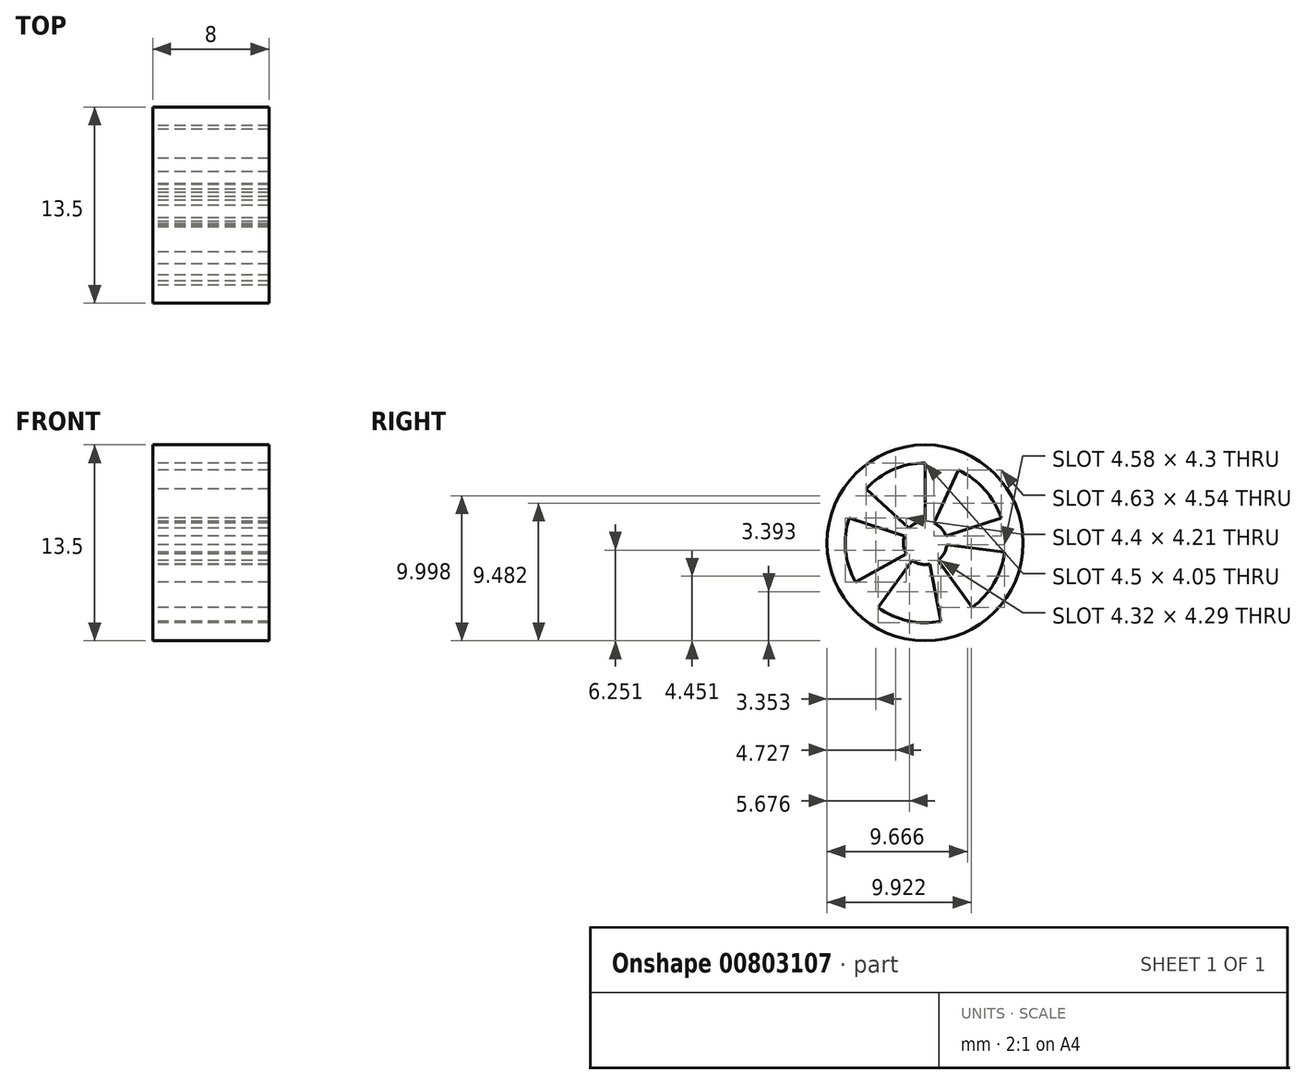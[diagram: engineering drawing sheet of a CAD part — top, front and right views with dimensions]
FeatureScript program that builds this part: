
annotation { "Feature Type Name" : "Feature", "Feature Type Description" : "" }
export const myFeature = defineFeature(function(context is Context, id is Id, definition is map)
    precondition{}
    {
        {
            var Q0;
            Q0=qCreatedBy(makeId("Right.planeOp"),FACE);
            var sketch = newSketch(context, id + "F0", { "sketchPlane" : qUnion([Q0])});
            skCircle(sketch, "E0", {"center": v(0, 0) * mm, "radius": 6.75 * mm});
            skSolve(sketch);
        }
        {
            var Q0;
            Q0=makeQuery(id+"F0.imprint","IMPRINT",FACE,{"disambiguationData":[TD([[makeQuery(id+"F0.imprint","IMPRINT",EDGE,{"derivedFrom":sQuery(id+"F0.wireOp",EDGE,"E0")}),1.0]])]});
            var sketch = newSketch(context, id + "F1", { "sketchPlane" : qUnion([Q0])});
            skCircle(sketch, "E1", {"center": v(0, 0) * mm, "radius": 5.5 * mm});
            skArc(sketch, "E2", {"start": v(0, 1.5) * mm, "mid": v(-0.3, -1.47) * mm, "end": v(0.6, 1.37) * mm});
            skLineSegment(sketch, "E3", {"start": v(0, 1.5) * mm, "end": v(0, 5.5) * mm});
            skLineSegment(sketch, "E4", {"start": v(0.6, 1.37) * mm, "end": v(2.3, 5) * mm});
            skLineSegment(sketch, "E5.1.0", {"start": v(-1.12, 1) * mm, "end": v(-4.05, 3.72) * mm});
            skLineSegment(sketch, "E5.1.1", {"start": v(-1.43, 0.46) * mm, "end": v(-5.23, 1.7) * mm});
            skLineSegment(sketch, "E5.2.0", {"start": v(-1.3, -0.76) * mm, "end": v(-4.8, -2.7) * mm});
            skLineSegment(sketch, "E5.2.1", {"start": v(-0.88, -1.21) * mm, "end": v(-3.23, -4.45) * mm});
            skLineSegment(sketch, "E5.3.0", {"start": v(0.32, -1.47) * mm, "end": v(1.08, -5.4) * mm});
            skLineSegment(sketch, "E5.3.1", {"start": v(0.88, -1.21) * mm, "end": v(3.23, -4.45) * mm});
            skLineSegment(sketch, "E5.4.0", {"start": v(1.5, -0.15) * mm, "end": v(5.46, -0.64) * mm});
            skLineSegment(sketch, "E5.4.1", {"start": v(1.43, 0.46) * mm, "end": v(5.23, 1.7) * mm});
            skSolve(sketch);
        }
        {
            var Q0;
            Q0=makeQuery(id+"F0.imprint","IMPRINT",FACE,{"disambiguationData":[TD([[makeQuery(id+"F0.imprint","IMPRINT",EDGE,{"derivedFrom":sQuery(id+"F0.wireOp",EDGE,"E0")}),1.0]])]});
            extrude(context, id + "F2", {"entities" : qUnion([Q0]), "depth" : 8 * mm, "offsetDistance" : 25 * mm});
        }
        {
            var Q0;
            {var subQ0=sQuery(id+"F1.wireOp",EDGE,"E5.2.1");Q0=makeQuery(id+"F1.imprint","IMPRINT",FACE,{"disambiguationData":[TD([[makeQuery(id+"F1.imprint","IMPRINT",EDGE,{"derivedFrom":subQ0}),1.0]])]});}
            var Q1;
            {var subQ0=sQuery(id+"F1.wireOp",EDGE,"E5.1.1");Q1=makeQuery(id+"F1.imprint","IMPRINT",FACE,{"disambiguationData":[TD([[makeQuery(id+"F1.imprint","IMPRINT",EDGE,{"derivedFrom":subQ0}),1.0]])]});}
            var Q2;
            {var subQ0=sQuery(id+"F1.wireOp",EDGE,"E3");Q2=makeQuery(id+"F1.imprint","IMPRINT",FACE,{"disambiguationData":[TD([[makeQuery(id+"F1.imprint","IMPRINT",EDGE,{"derivedFrom":subQ0}),1.0]])]});}
            var Q3;
            {var subQ0=sQuery(id+"F1.wireOp",EDGE,"E4");Q3=makeQuery(id+"F1.imprint","IMPRINT",FACE,{"disambiguationData":[TD([[makeQuery(id+"F1.imprint","IMPRINT",EDGE,{"derivedFrom":subQ0}),-1.0]])]});}
            var Q4;
            {var subQ0=sQuery(id+"F1.wireOp",EDGE,"E5.3.1");Q4=makeQuery(id+"F1.imprint","IMPRINT",FACE,{"disambiguationData":[TD([[makeQuery(id+"F1.imprint","IMPRINT",EDGE,{"derivedFrom":subQ0}),1.0]])]});}
            extrude(context, id + "F3", {"entities" : qUnion([Q0, Q1, Q2, Q3, Q4]), "operationType" : NewBodyOperationType.REMOVE, "endBound" : BoundingType.THROUGH_ALL, "depth" : 25 * mm, "offsetDistance" : 25 * mm});
        }
    });
